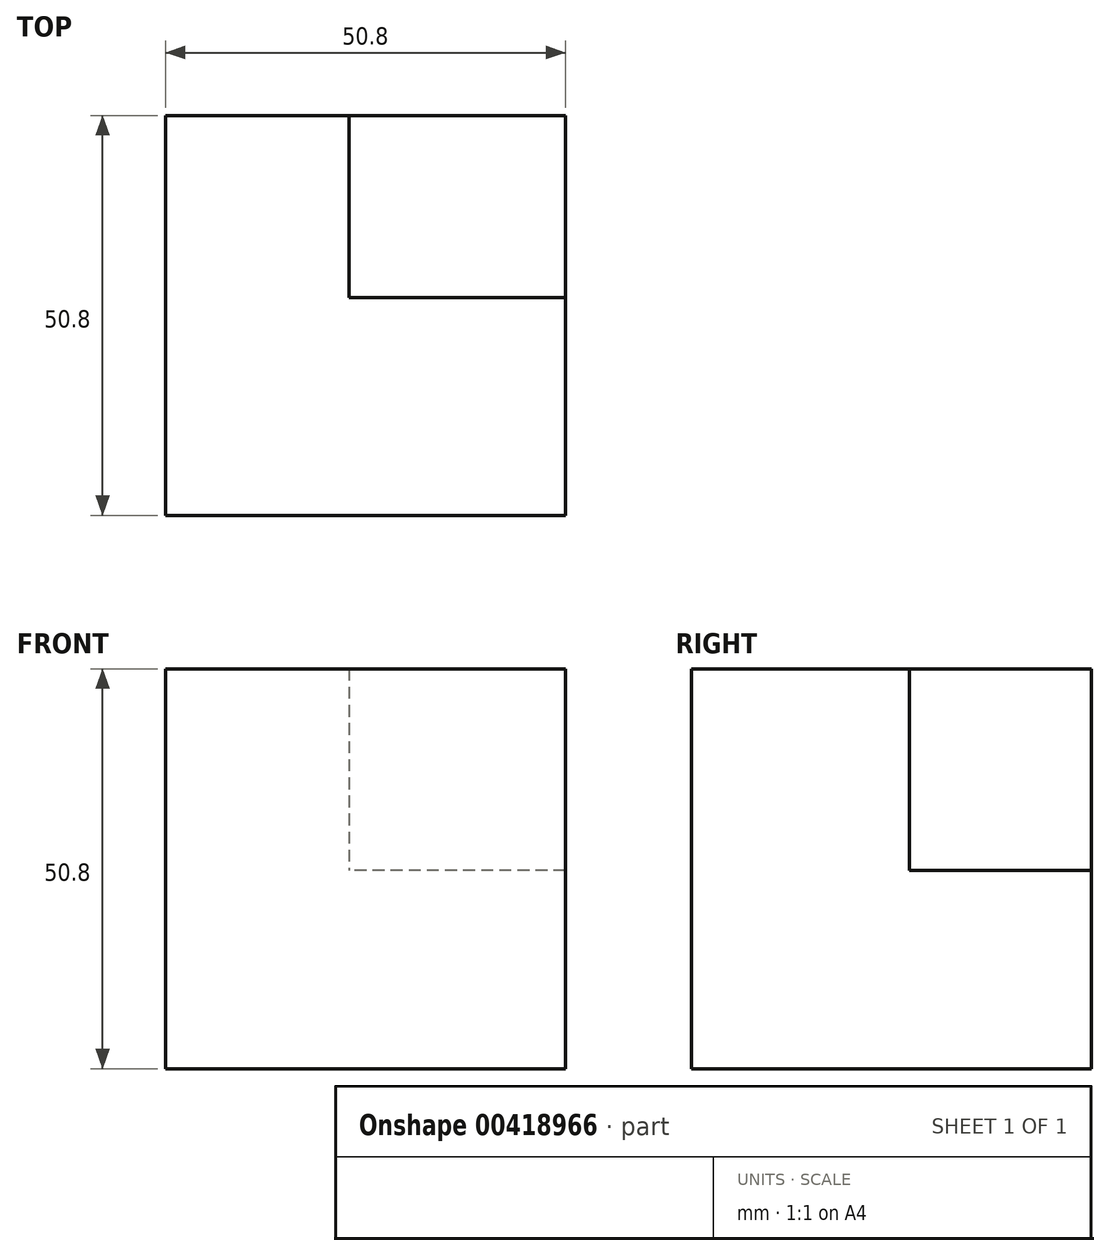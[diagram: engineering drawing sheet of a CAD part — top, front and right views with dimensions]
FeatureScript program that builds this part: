
annotation { "Feature Type Name" : "Feature", "Feature Type Description" : "" }
export const myFeature = defineFeature(function(context is Context, id is Id, definition is map)
    precondition{}
    {
        {
            var Q0;
            Q0=qCreatedBy(makeId("Front.planeOp"),FACE);
            var sketch = newSketch(context, id + "F0", { "sketchPlane" : qUnion([Q0])});
            skLineSegment(sketch, "E0.bottom", {"start": v(0, 0) * mm, "end": v(-50.8, 0) * mm});
            skLineSegment(sketch, "E0.top", {"start": v(0, 50.8) * mm, "end": v(-50.8, 50.8) * mm});
            skLineSegment(sketch, "E0.left", {"start": v(0, 0) * mm, "end": v(0, 50.8) * mm});
            skLineSegment(sketch, "E0.right", {"start": v(-50.8, 0) * mm, "end": v(-50.8, 50.8) * mm});
            skSolve(sketch);
        }
        {
            var Q0;
            Q0 = qSketchRegion(id + "F0", true);
            extrude(context, id + "F1", {"entities" : qUnion([Q0]), "depth" : 50.8 * mm});
        }
        {
            var Q0;
            Q0=qCreatedBy(makeId("Front.planeOp"),FACE);
            var sketch = newSketch(context, id + "F2", { "sketchPlane" : qUnion([Q0])});
            skLineSegment(sketch, "E1.bottom", {"start": v(0, 50.8) * mm, "end": v(-27.5, 50.8) * mm});
            skLineSegment(sketch, "E1.top", {"start": v(0, 25.2) * mm, "end": v(-27.5, 25.2) * mm});
            skLineSegment(sketch, "E1.left", {"start": v(0, 50.8) * mm, "end": v(0, 25.2) * mm});
            skLineSegment(sketch, "E1.right", {"start": v(-27.5, 50.8) * mm, "end": v(-27.5, 25.2) * mm});
            skSolve(sketch);
        }
        {
            var Q0;
            Q0=makeQuery(id+"F2.imprint","IMPRINT",FACE,{"disambiguationData":[TD([[makeQuery(id+"F2.imprint","IMPRINT",EDGE,{"derivedFrom":sQuery(id+"F2.wireOp",EDGE,"E1.bottom")}),1.0]])]});
            extrude(context, id + "F3", {"entities" : qUnion([Q0]), "operationType" : NewBodyOperationType.REMOVE, "depth" : 23.1 * mm});
        }
    });
